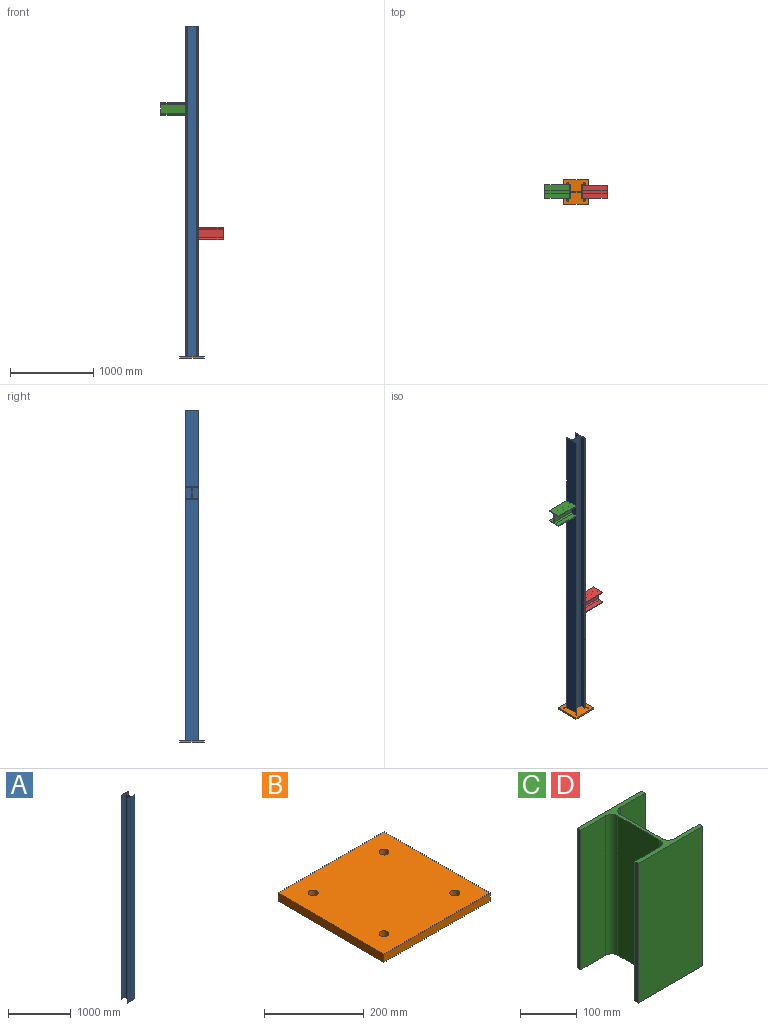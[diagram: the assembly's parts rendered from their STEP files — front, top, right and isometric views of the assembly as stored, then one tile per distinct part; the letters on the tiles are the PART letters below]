
ASSEMBLY  parts=4 mates=3
PART A: 18 faces, bbox 160x152x3980 mm
  f0: plane 3980x9mm, normal (-1,0,0), area 35820mm2, adj f1,f15,f16,f17
  f1: plane 3980x62mm, normal (0,1,0), area 246760mm2, adj f0,f2,f16,f17
  f2: cylinder r=15mm len=3980mm, axis (0,0,1), area 93776.5mm2, adj f1,f3,f16,f17
  f3: plane 3980x104mm, normal (-1,0,0), area 413920mm2, adj f2,f4,f16,f17
  f4: cylinder r=15mm len=3980mm, axis (0,0,1), area 93776.5mm2, adj f3,f5,f16,f17
  f5: plane 3980x62mm, normal (0,-1,0), area 246760mm2, adj f4,f6,f16,f17
  f6: plane 3980x9mm, normal (-1,0,0), area 35820mm2, adj f5,f7,f16,f17
  f7: plane 3980x160mm, normal (0,1,0), area 636800mm2, adj f6,f8,f16,f17
  f8: plane 3980x9mm, normal (1,0,0), area 35820mm2, adj f7,f9,f16,f17
  f9: plane 3980x62mm, normal (0,-1,0), area 246760mm2, adj f8,f10,f16,f17
  f10: cylinder r=15mm len=3980mm, axis (0,0,1), area 93776.5mm2, adj f9,f11,f16,f17
  f11: plane 3980x104mm, normal (1,0,0), area 413920mm2, adj f10,f12,f16,f17
  f12: cylinder r=15mm len=3980mm, axis (0,0,1), area 93776.5mm2, adj f11,f13,f16,f17
  f13: plane 3980x62mm, normal (0,1,0), area 246760mm2, adj f12,f14,f16,f17
  f14: plane 3980x9mm, normal (1,0,0), area 35820mm2, adj f13,f15,f16,f17
  f15: plane 3980x160mm, normal (0,-1,0), area 636800mm2, adj f0,f14,f16,f17
  f16: plane 160x152mm, normal (0,0,1), area 3877.1mm2, adj f0,f1,f2,f3,f4,f5,f6,f7
  f17: plane 160x152mm, normal (0,0,-1), area 3877.1mm2, adj f0,f1,f2,f3,f4,f5,f6,f7
PART B: 10 faces, bbox 300x300x20 mm
  f0: plane 300x20mm, normal (1,0,0), area 6000mm2, adj f1,f6,f8,f9
  f1: plane 300x20mm, normal (0,1,0), area 6000mm2, adj f0,f2,f8,f9
  f2: plane 300x20mm, normal (-1,0,0), area 6000mm2, adj f1,f6,f8,f9
  f3: cylinder r=10mm len=20mm, axis (0,0,-1), area 1256.6mm2, adj f8,f9
  f4: cylinder r=10mm len=20mm, axis (0,0,-1), area 1256.6mm2, adj f8,f9
  f5: cylinder r=10mm len=20mm, axis (0,0,-1), area 1256.6mm2, adj f8,f9
  f6: plane 300x20mm, normal (0,-1,0), area 6000mm2, adj f0,f2,f8,f9
  f7: cylinder r=10mm len=20mm, axis (0,0,-1), area 1256.6mm2, adj f8,f9
  f8: plane 300x300mm, normal (0,0,1), area 88743.4mm2, adj f0,f1,f2,f3,f4,f5,f6,f7
  f9: plane 300x300mm, normal (0,0,-1), area 88743.4mm2, adj f0,f1,f2,f3,f4,f5,f6,f7
PART C: 18 faces, bbox 160x152x300 mm
  f0: plane 300x9mm, normal (-1,0,0), area 2700mm2, adj f1,f15,f16,f17
  f1: plane 300x62mm, normal (0,1,0), area 18600mm2, adj f0,f2,f16,f17
  f2: cylinder r=15mm len=300mm, axis (0,0,1), area 7068.6mm2, adj f1,f3,f16,f17
  f3: plane 300x104mm, normal (-1,0,0), area 31200mm2, adj f2,f4,f16,f17
  f4: cylinder r=15mm len=300mm, axis (0,0,1), area 7068.6mm2, adj f3,f5,f16,f17
  f5: plane 300x62mm, normal (0,-1,0), area 18600mm2, adj f4,f6,f16,f17
  f6: plane 300x9mm, normal (-1,0,0), area 2700mm2, adj f5,f7,f16,f17
  f7: plane 300x160mm, normal (0,1,0), area 48000mm2, adj f6,f8,f16,f17
  f8: plane 300x9mm, normal (1,0,0), area 2700mm2, adj f7,f9,f16,f17
  f9: plane 300x62mm, normal (0,-1,0), area 18600mm2, adj f8,f10,f16,f17
  f10: cylinder r=15mm len=300mm, axis (0,0,1), area 7068.6mm2, adj f9,f11,f16,f17
  f11: plane 300x104mm, normal (1,0,0), area 31200mm2, adj f10,f12,f16,f17
  f12: cylinder r=15mm len=300mm, axis (0,0,1), area 7068.6mm2, adj f11,f13,f16,f17
  f13: plane 300x62mm, normal (0,1,0), area 18600mm2, adj f12,f14,f16,f17
  f14: plane 300x9mm, normal (1,0,0), area 2700mm2, adj f13,f15,f16,f17
  f15: plane 300x160mm, normal (0,-1,0), area 48000mm2, adj f0,f14,f16,f17
  f16: plane 160x152mm, normal (0,0,1), area 3877.1mm2, adj f0,f1,f2,f3,f4,f5,f6,f7
  f17: plane 160x152mm, normal (0,0,-1), area 3877.1mm2, adj f0,f1,f2,f3,f4,f5,f6,f7
PART D: same geometry as C
PLACE A rot(axis=(0,0,1),90deg) t=(0,0,2010)mm
PLACE B at identity
PLACE C rot(axis=(0.58,0.58,0.58),120deg) t=(-226,0,3000)mm
PLACE D rot(axis=(0.58,0.58,0.58),120deg) t=(226,0,1500)mm
MATE fastened D.f17 <-> A.f15  axis (-1,0,0) through (76,0,1500)mm
MATE fastened A.f17 <-> B.f8  axis (0,0,-1) through (0,0,20)mm
MATE fastened C.f16 <-> A.f7  axis (1,0,0) through (-76,0,3000)mm
